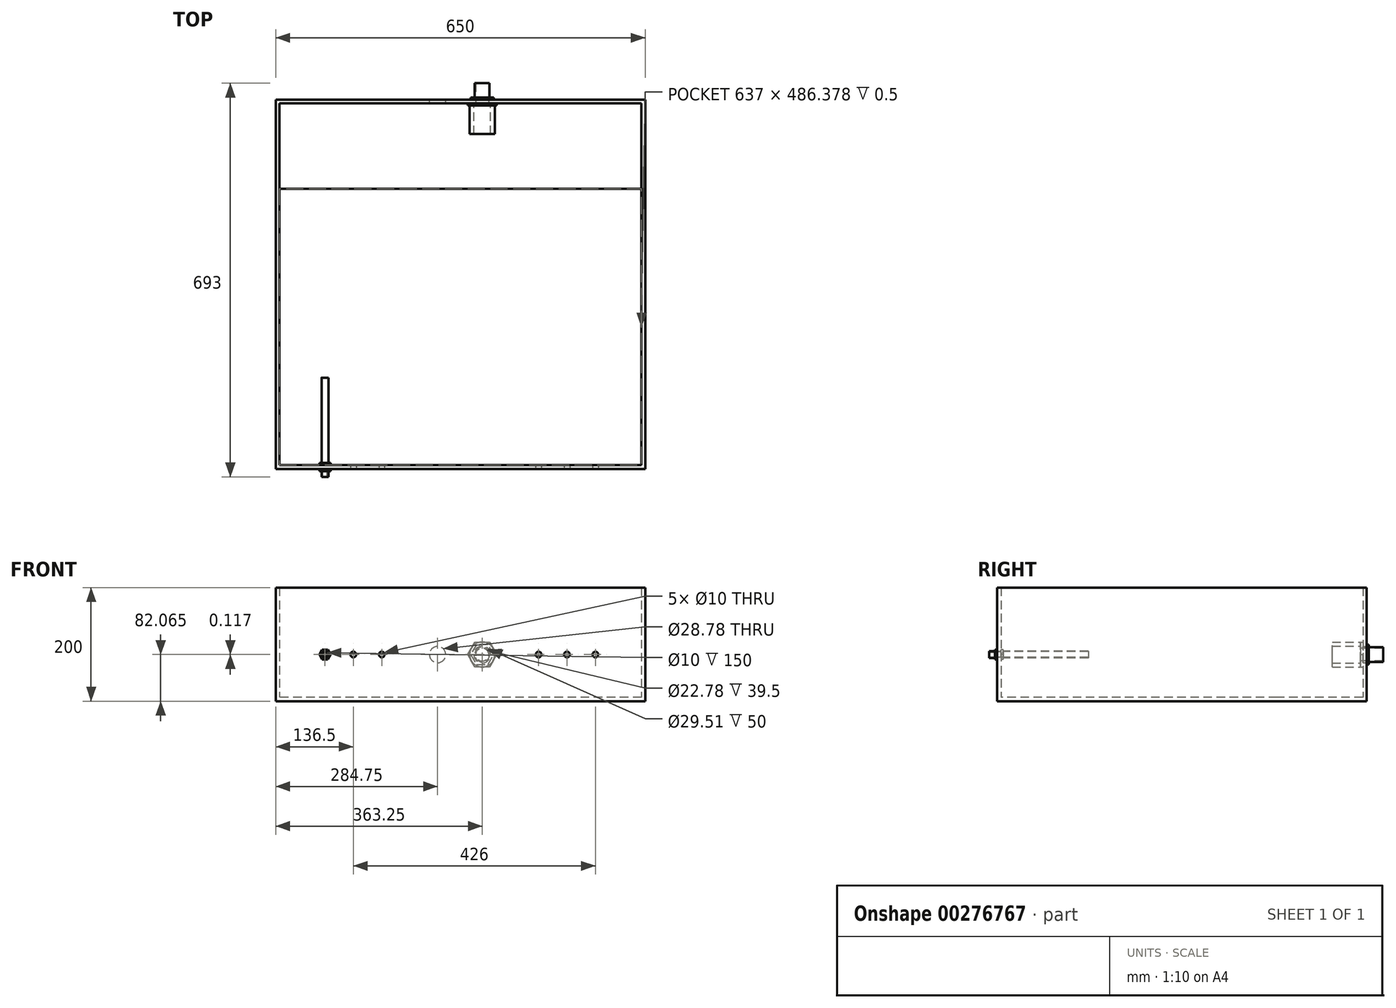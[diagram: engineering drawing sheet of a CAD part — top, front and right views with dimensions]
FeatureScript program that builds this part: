
annotation { "Feature Type Name" : "Feature", "Feature Type Description" : "" }
export const myFeature = defineFeature(function(context is Context, id is Id, definition is map)
    precondition{}
    {
        {
            var Q0;
            Q0=qCreatedBy(makeId("Top.planeOp"),FACE);
            var sketch = newSketch(context, id + "F0", { "sketchPlane" : qUnion([Q0])});
            skLineSegment(sketch, "E0.bottom", {"start": v(325, 325) * mm, "end": v(-325, 325) * mm});
            skLineSegment(sketch, "E0.top", {"start": v(325, -325) * mm, "end": v(-325, -325) * mm});
            skLineSegment(sketch, "E0.left", {"start": v(325, 325) * mm, "end": v(325, -325) * mm});
            skLineSegment(sketch, "E0.right", {"start": v(-325, 325) * mm, "end": v(-325, -325) * mm});
            skPoint(sketch, "E0.middle", {"position": v(0, 0) * mm});
            skSolve(sketch);
        }
        {
            var Q0;
            Q0=makeQuery(id+"F0.imprint","IMPRINT",FACE,{"disambiguationData":[TD([[makeQuery(id+"F0.imprint","IMPRINT",EDGE,{"derivedFrom":sQuery(id+"F0.wireOp",EDGE,"cca13281-c8a4-43dd-b4c7-58c42d9eb948.0")}),1.0]])]});
            var Q1;
            Q1=makeQuery(id+"F0.imprint","IMPRINT",FACE,{"disambiguationData":[TD([[makeQuery(id+"F0.imprint","IMPRINT",EDGE,{"derivedFrom":sQuery(id+"F0.wireOp",EDGE,"E0.bottom")}),1.0]])]});
            extrude(context, id + "F1", {"entities" : qUnion([Q0, Q1]), "depth" : 200 * mm});
        }
        {
            var Q0;
            Q0=makeQuery(id+"F1.opExtrude","CAP_FACE",FACE,{"disambiguationData":[OSD([sQuery(id+"F0.wireOp",EDGE,"E0.bottom"),sQuery(id+"F0.wireOp",EDGE,"E0.top"),sQuery(id+"F0.wireOp",EDGE,"E0.left"),sQuery(id+"F0.wireOp",EDGE,"E0.right")])],"isStart":false});
            shell(context, id + "F2", {"entities" : qUnion([Q0]), "thickness" : 2.5 * mm});
        }
        {
            var Q0;
            Q0=makeQuery(id+"F2.opShell","OFFSET_FACE",FACE,{"disambiguationData":[OSD([sQuery(id+"F0.wireOp",EDGE,"E0.bottom"),sQuery(id+"F0.wireOp",EDGE,"E0.top"),sQuery(id+"F0.wireOp",EDGE,"E0.left"),sQuery(id+"F0.wireOp",EDGE,"E0.right")])]});
            extrude(context, id + "F3", {"entities" : qUnion([Q0]), "depth" : 197.5 * mm});
        }
        {
            var Q0;
            Q0=makeQuery(id+"F3.opExtrude","CAP_FACE",FACE,{"disambiguationData":[OSD([sQuery(id+"F0.wireOp",EDGE,"E0.bottom"),sQuery(id+"F0.wireOp",EDGE,"E0.top"),sQuery(id+"F0.wireOp",EDGE,"E0.left"),sQuery(id+"F0.wireOp",EDGE,"E0.right")])],"isStart":false});
            shell(context, id + "F4", {"entities" : qUnion([Q0]), "thickness" : 4 * mm});
        }
        {
            var Q0;
            Q0=makeQuery(id+"F4.opShell","OFFSET_FACE",FACE,{"disambiguationData":[OSD([sQuery(id+"F0.wireOp",EDGE,"E0.bottom"),sQuery(id+"F0.wireOp",EDGE,"E0.top"),sQuery(id+"F0.wireOp",EDGE,"E0.left"),sQuery(id+"F0.wireOp",EDGE,"E0.right")])]});
            var sketch = newSketch(context, id + "F5", { "sketchPlane" : qUnion([Q0])});
            skLineSegment(sketch, "E1.bottom", {"start": v(450, 167.88) * mm, "end": v(-450, 167.88) * mm});
            skLineSegment(sketch, "E1.top", {"start": v(450, -167.88) * mm, "end": v(-450, -167.88) * mm});
            skLineSegment(sketch, "E1.left", {"start": v(450, 167.88) * mm, "end": v(450, -167.88) * mm});
            skLineSegment(sketch, "E1.right", {"start": v(-450, 167.88) * mm, "end": v(-450, -167.88) * mm});
            skPoint(sketch, "E1.middle", {"position": v(0, 0) * mm});
            skLineSegment(sketch, "E2.bottom", {"start": v(318.5, 318.5) * mm, "end": v(-318.5, 318.5) * mm});
            skLineSegment(sketch, "E2.top", {"start": v(318.5, -318.5) * mm, "end": v(-318.5, -318.5) * mm});
            skLineSegment(sketch, "E2.left", {"start": v(318.5, 318.5) * mm, "end": v(318.5, -318.5) * mm});
            skLineSegment(sketch, "E2.right", {"start": v(-318.5, 318.5) * mm, "end": v(-318.5, -318.5) * mm});
            skSolve(sketch);
        }
        {
            var Q0;
            Q0=makeQuery(id+"F5.imprint","IMPRINT",FACE,{"disambiguationData":[TD([[makeQuery(id+"F5.imprint","IMPRINT",EDGE,{"derivedFrom":sQuery(id+"F5.wireOp",EDGE,"E1.bottom")}),-1.0]])]});
            extrude(context, id + "F6", {"entities" : qUnion([Q0]), "operationType" : NewBodyOperationType.ADD, "depth" : 0.5 * mm});
        }
        {
            var Q0;
            Q0=makeQuery(id+"F1.opExtrude","SWEPT_FACE",FACE,{"disambiguationData":[OSD([sQuery(id+"F0.wireOp",EDGE,"E0.top")])]});
            var sketch = newSketch(context, id + "F7", { "sketchPlane" : qUnion([Q0])});
            skLineSegment(sketch, "E3.top", {"start": v(300, 6.5) * mm, "end": v(-300, 6.5) * mm, "construction": true});
            skPoint(sketch, "E3.middle", {"position": v(0, 100) * mm});
            skPoint(sketch, "E3.middle.positionSnap0", {"position": v(-325, 100) * mm});
            skPoint(sketch, "E3.centerSnap0", {"position": v(-325, 100) * mm});
            skLineSegment(sketch, "E4", {"start": v(-300, 6.5) * mm, "end": v(-300, 251.45) * mm, "construction": true});
            skLineSegment(sketch, "E5", {"start": v(-300, 251.45) * mm, "end": v(300, 251.45) * mm, "construction": true});
            skLineSegment(sketch, "E6", {"start": v(300, 251.45) * mm, "end": v(300, 6.5) * mm, "construction": true});
            skLineSegment(sketch, "E7", {"start": v(-300, 82.18) * mm, "end": v(-238.5, 82.18) * mm, "construction": true});
            skLineSegment(sketch, "E8", {"start": v(-238.5, 82.18) * mm, "end": v(-238.5, 6.5) * mm, "construction": true});
            skCircle(sketch, "E9", {"center": v(-238.5, 82.18) * mm, "radius": 5 * mm});
            skCircle(sketch, "E10.1.0.0", {"center": v(-188.5, 82.18) * mm, "radius": 5 * mm});
            skCircle(sketch, "E10.2.0.0", {"center": v(-138.5, 82.18) * mm, "radius": 5 * mm});
            skLineSegment(sketch, "E10.direction1", {"start": v(-238.5, 82.18) * mm, "end": v(-188.5, 82.18) * mm, "construction": true});
            skLineSegment(sketch, "E11", {"start": v(300, 82.07) * mm, "end": v(237.5, 82.07) * mm, "construction": true});
            skLineSegment(sketch, "E12", {"start": v(237.5, 82.07) * mm, "end": v(237.5, 6.5) * mm, "construction": true});
            skCircle(sketch, "E13", {"center": v(237.5, 82.07) * mm, "radius": 5 * mm});
            skCircle(sketch, "E14.1.0.0", {"center": v(187.5, 82.07) * mm, "radius": 5 * mm});
            skCircle(sketch, "E14.2.0.0", {"center": v(137.5, 82.07) * mm, "radius": 5 * mm});
            skLineSegment(sketch, "E14.direction1", {"start": v(237.5, 82.07) * mm, "end": v(187.5, 82.07) * mm, "construction": true});
            skSolve(sketch);
        }
        {
            var Q0;
            Q0=qSketchRegion(id+"F7",true);
            extrude(context, id + "F8", {"entities" : qUnion([Q0]), "operationType" : NewBodyOperationType.REMOVE, "oppositeDirection" : true, "depth" : 25 * mm});
        }
        {
            var Q0;
            Q0=makeQuery(id+"F1.opExtrude","SWEPT_FACE",FACE,{"disambiguationData":[OSD([sQuery(id+"F0.wireOp",EDGE,"E0.bottom")])]});
            var sketch = newSketch(context, id + "F9", { "sketchPlane" : qUnion([Q0])});
            skLineSegment(sketch, "E15", {"start": v(-300, 251.45) * mm, "end": v(-300, 6.5) * mm, "construction": true});
            skLineSegment(sketch, "E16", {"start": v(-300, 6.5) * mm, "end": v(300, 6.5) * mm, "construction": true});
            skLineSegment(sketch, "E17", {"start": v(300, 6.5) * mm, "end": v(300, 251.45) * mm, "construction": true});
            skLineSegment(sketch, "E18", {"start": v(300, 251.45) * mm, "end": v(-300, 251.45) * mm, "construction": true});
            skLineSegment(sketch, "E19", {"start": v(40.25, 6.5) * mm, "end": v(40.25, 82.07) * mm, "construction": true});
            skLineSegment(sketch, "E20", {"start": v(40.25, 82.06) * mm, "end": v(300, 82.07) * mm, "construction": true});
            skCircle(sketch, "E21", {"center": v(40.25, 82.07) * mm, "radius": 14.39 * mm});
            skCircle(sketch, "E22.1.0.0", {"center": v(-38.25, 82.07) * mm, "radius": 14.39 * mm});
            skLineSegment(sketch, "E22.direction1", {"start": v(40.25, 82.07) * mm, "end": v(-38.25, 82.07) * mm, "construction": true});
            skSolve(sketch);
        }
        {
            var Q0;
            Q0=qSketchRegion(id+"F9",true);
            extrude(context, id + "F10", {"entities" : qUnion([Q0]), "operationType" : NewBodyOperationType.REMOVE, "oppositeDirection" : true, "depth" : 15 * mm});
        }
        {
            var Q0;
            Q0=makeQuery(id+"F1.opExtrude","SWEPT_FACE",FACE,{"disambiguationData":[OSD([sQuery(id+"F0.wireOp",EDGE,"E0.top")])]});
            var sketch = newSketch(context, id + "F11", { "sketchPlane" : qUnion([Q0])});
            skCircle(sketch, "E23", {"center": v(-238.5, 82.18) * mm, "radius": 4 * mm});
            skCircle(sketch, "E24.cCircle", {"center": v(-238.5, 82.18) * mm, "radius": 8.5 * mm, "construction": true});
            skLineSegment(sketch, "E24.0", {"start": v(-243.4, 90.68) * mm, "end": v(-233.6, 90.68) * mm});
            skLineSegment(sketch, "E24.1", {"start": v(-233.6, 90.68) * mm, "end": v(-228.69, 82.18) * mm});
            skLineSegment(sketch, "E24.2", {"start": v(-228.69, 82.18) * mm, "end": v(-233.6, 73.68) * mm});
            skLineSegment(sketch, "E24.3", {"start": v(-233.6, 73.68) * mm, "end": v(-243.4, 73.68) * mm});
            skLineSegment(sketch, "E24.4", {"start": v(-243.4, 73.68) * mm, "end": v(-248.31, 82.18) * mm});
            skLineSegment(sketch, "E24.5", {"start": v(-248.31, 82.18) * mm, "end": v(-243.4, 90.68) * mm});
            skPoint(sketch, "E24.0.midPoint", {"position": v(-238.5, 90.68) * mm});
            skSolve(sketch);
        }
        {
            var Q0;
            Q0=qSketchRegion(id+"F11",true);
            extrude(context, id + "F12", {"entities" : qUnion([Q0]), "depth" : 4 * mm});
        }
        {
            var Q0;
            Q0=makeQuery(id+"F12.opExtrude","CAP_FACE",FACE,{"disambiguationData":[OSD([sQuery(id+"F11.wireOp",EDGE,"E23"),sQuery(id+"F11.wireOp",EDGE,"E24.0"),sQuery(id+"F11.wireOp",EDGE,"E24.1"),sQuery(id+"F11.wireOp",EDGE,"E24.2"),sQuery(id+"F11.wireOp",EDGE,"E24.3"),sQuery(id+"F11.wireOp",EDGE,"E24.4"),sQuery(id+"F11.wireOp",EDGE,"E24.5")])],"isStart":false});
            var sketch = newSketch(context, id + "F13", { "sketchPlane" : qUnion([Q0])});
            skCircle(sketch, "E25", {"center": v(-238.5, 82.18) * mm, "radius": 6 * mm});
            skCircle(sketch, "E26", {"center": v(-238.5, 82.18) * mm, "radius": 4 * mm});
            skSolve(sketch);
        }
        {
            var Q0;
            Q0=qSketchRegion(id+"F13",true);
            extrude(context, id + "F14", {"entities" : qUnion([Q0]), "operationType" : NewBodyOperationType.ADD, "depth" : 10 * mm});
        }
        {
            var Q0;
            Q0=makeQuery(id+"F12.opExtrude","CAP_FACE",FACE,{"disambiguationData":[OSD([sQuery(id+"F11.wireOp",EDGE,"E23"),sQuery(id+"F11.wireOp",EDGE,"E24.0"),sQuery(id+"F11.wireOp",EDGE,"E24.1"),sQuery(id+"F11.wireOp",EDGE,"E24.2"),sQuery(id+"F11.wireOp",EDGE,"E24.3"),sQuery(id+"F11.wireOp",EDGE,"E24.4"),sQuery(id+"F11.wireOp",EDGE,"E24.5")])],"isStart":true});
            var sketch = newSketch(context, id + "F15", { "sketchPlane" : qUnion([Q0])});
            skCircle(sketch, "E27", {"center": v(238.5, 82.18) * mm, "radius": 5 * mm});
            skCircle(sketch, "E28", {"center": v(238.5, 82.18) * mm, "radius": 4 * mm});
            skSolve(sketch);
        }
        {
            var Q0;
            Q0=qSketchRegion(id+"F15",true);
            extrude(context, id + "F16", {"entities" : qUnion([Q0]), "operationType" : NewBodyOperationType.ADD, "depth" : 6.5 * mm});
        }
        {
            var Q0;
            Q0=makeQuery(id+"F16.opExtrude","CAP_FACE",FACE,{"disambiguationData":[OSD([sQuery(id+"F15.wireOp",EDGE,"E27"),sQuery(id+"F15.wireOp",EDGE,"E28")])],"isStart":false});
            var sketch = newSketch(context, id + "F17", { "sketchPlane" : qUnion([Q0])});
            skCircle(sketch, "E29.cCircle", {"center": v(238.5, 82.18) * mm, "radius": 8.5 * mm, "construction": true});
            skLineSegment(sketch, "E29.0", {"start": v(233.6, 90.68) * mm, "end": v(243.4, 90.68) * mm});
            skLineSegment(sketch, "E29.1", {"start": v(243.4, 90.68) * mm, "end": v(248.31, 82.18) * mm});
            skLineSegment(sketch, "E29.2", {"start": v(248.31, 82.18) * mm, "end": v(243.4, 73.68) * mm});
            skLineSegment(sketch, "E29.3", {"start": v(243.4, 73.68) * mm, "end": v(233.6, 73.68) * mm});
            skLineSegment(sketch, "E29.4", {"start": v(233.6, 73.68) * mm, "end": v(228.69, 82.18) * mm});
            skLineSegment(sketch, "E29.5", {"start": v(228.69, 82.18) * mm, "end": v(233.6, 90.68) * mm});
            skPoint(sketch, "E29.0.midPoint", {"position": v(238.5, 90.68) * mm});
            skCircle(sketch, "E30", {"center": v(238.5, 82.18) * mm, "radius": 4 * mm});
            skSolve(sketch);
        }
        {
            var Q0;
            Q0=makeQuery(id+"F17.imprint","IMPRINT",FACE,{"disambiguationData":[TD([[makeQuery(id+"F17.imprint","IMPRINT",EDGE,{"derivedFrom":sQuery(id+"F17.wireOp",EDGE,"E30")}),1.0]])]});
            var Q1;
            Q1=makeQuery(id+"F17.imprint","IMPRINT",FACE,{"disambiguationData":[TD([[makeQuery(id+"F17.imprint","IMPRINT",EDGE,{"derivedFrom":sQuery(id+"F17.wireOp",EDGE,"E29.0")}),-1.0]])]});
            extrude(context, id + "F18", {"entities" : qUnion([Q0, Q1]), "operationType" : NewBodyOperationType.ADD, "depth" : 4 * mm});
        }
        {
            var Q0;
            Q0=makeQuery(id+"F18.opExtrude","CAP_FACE",FACE,{"disambiguationData":[OSD([sQuery(id+"F17.wireOp",EDGE,"E29.0"),sQuery(id+"F17.wireOp",EDGE,"E29.1"),sQuery(id+"F17.wireOp",EDGE,"E29.2"),sQuery(id+"F17.wireOp",EDGE,"E29.3"),sQuery(id+"F17.wireOp",EDGE,"E29.4"),sQuery(id+"F17.wireOp",EDGE,"E29.5"),sQuery(id+"F17.wireOp",EDGE,"E30")])],"isStart":false});
            var sketch = newSketch(context, id + "F19", { "sketchPlane" : qUnion([Q0])});
            skCircle(sketch, "E31", {"center": v(238.5, 82.18) * mm, "radius": 6 * mm});
            skCircle(sketch, "E32", {"center": v(238.5, 82.18) * mm, "radius": 5 * mm});
            skSolve(sketch);
        }
        {
            var Q0;
            Q0=qSketchRegion(id+"F19",true);
            extrude(context, id + "F20", {"entities" : qUnion([Q0]), "operationType" : NewBodyOperationType.ADD, "depth" : 150 * mm});
        }
        {
            var Q0;
            Q0=makeQuery(id+"F1.opExtrude","SWEPT_FACE",FACE,{"disambiguationData":[OSD([sQuery(id+"F0.wireOp",EDGE,"E0.bottom")])]});
            var sketch = newSketch(context, id + "F21", { "sketchPlane" : qUnion([Q0])});
            skCircle(sketch, "E33", {"center": v(-38.25, 82.07) * mm, "radius": 11.39 * mm});
            skCircle(sketch, "E34.cCircle", {"center": v(-38.25, 82.07) * mm, "radius": 17.48 * mm, "construction": true});
            skLineSegment(sketch, "E34.0", {"start": v(-48.34, 99.55) * mm, "end": v(-28.16, 99.55) * mm});
            skLineSegment(sketch, "E34.1", {"start": v(-28.16, 99.55) * mm, "end": v(-18.07, 82.07) * mm});
            skLineSegment(sketch, "E34.2", {"start": v(-18.07, 82.07) * mm, "end": v(-28.16, 64.58) * mm});
            skLineSegment(sketch, "E34.3", {"start": v(-28.16, 64.58) * mm, "end": v(-48.34, 64.58) * mm});
            skLineSegment(sketch, "E34.4", {"start": v(-48.34, 64.58) * mm, "end": v(-58.43, 82.06) * mm});
            skLineSegment(sketch, "E34.5", {"start": v(-58.43, 82.06) * mm, "end": v(-48.34, 99.55) * mm});
            skPoint(sketch, "E34.0.midPoint", {"position": v(-38.25, 99.55) * mm});
            skSolve(sketch);
        }
        {
            var Q0;
            Q0=qSketchRegion(id+"F21",true);
            extrude(context, id + "F22", {"entities" : qUnion([Q0]), "depth" : 4 * mm});
        }
        {
            var Q0;
            Q0=makeQuery(id+"F22.opExtrude","CAP_FACE",FACE,{"disambiguationData":[OSD([sQuery(id+"F21.wireOp",EDGE,"E33"),sQuery(id+"F21.wireOp",EDGE,"E34.0"),sQuery(id+"F21.wireOp",EDGE,"E34.1"),sQuery(id+"F21.wireOp",EDGE,"E34.2"),sQuery(id+"F21.wireOp",EDGE,"E34.3"),sQuery(id+"F21.wireOp",EDGE,"E34.4"),sQuery(id+"F21.wireOp",EDGE,"E34.5")])],"isStart":false});
            var sketch = newSketch(context, id + "F23", { "sketchPlane" : qUnion([Q0])});
            skCircle(sketch, "E35", {"center": v(-38.25, 82.07) * mm, "radius": 13.03 * mm});
            skCircle(sketch, "E36", {"center": v(-38.25, 82.07) * mm, "radius": 11.39 * mm});
            skSolve(sketch);
        }
        {
            var Q0;
            Q0=qSketchRegion(id+"F23",true);
            extrude(context, id + "F24", {"entities" : qUnion([Q0]), "operationType" : NewBodyOperationType.ADD, "depth" : 25 * mm});
        }
        {
            var Q0;
            Q0=makeQuery(id+"F22.opExtrude","CAP_FACE",FACE,{"disambiguationData":[OSD([sQuery(id+"F21.wireOp",EDGE,"E33"),sQuery(id+"F21.wireOp",EDGE,"E34.0"),sQuery(id+"F21.wireOp",EDGE,"E34.1"),sQuery(id+"F21.wireOp",EDGE,"E34.2"),sQuery(id+"F21.wireOp",EDGE,"E34.3"),sQuery(id+"F21.wireOp",EDGE,"E34.4"),sQuery(id+"F21.wireOp",EDGE,"E34.5")])],"isStart":true});
            var sketch = newSketch(context, id + "F25", { "sketchPlane" : qUnion([Q0])});
            skCircle(sketch, "E37", {"center": v(38.25, 82.07) * mm, "radius": 14.39 * mm});
            skCircle(sketch, "E38", {"center": v(38.25, 82.07) * mm, "radius": 11.39 * mm});
            skSolve(sketch);
        }
        {
            var Q0;
            Q0=qSketchRegion(id+"F25",true);
            extrude(context, id + "F26", {"entities" : qUnion([Q0]), "operationType" : NewBodyOperationType.ADD, "depth" : 6.5 * mm});
        }
        {
            var Q0;
            Q0=makeQuery(id+"F26.opExtrude","CAP_FACE",FACE,{"disambiguationData":[OSD([sQuery(id+"F25.wireOp",EDGE,"E37"),sQuery(id+"F25.wireOp",EDGE,"E38")])],"isStart":false});
            var sketch = newSketch(context, id + "F27", { "sketchPlane" : qUnion([Q0])});
            skCircle(sketch, "E39.cCircle", {"center": v(38.25, 82.07) * mm, "radius": 22 * mm, "construction": true});
            skLineSegment(sketch, "E39.0", {"start": v(25.55, 104.07) * mm, "end": v(50.95, 104.07) * mm});
            skLineSegment(sketch, "E39.1", {"start": v(50.95, 104.07) * mm, "end": v(63.66, 82.07) * mm});
            skLineSegment(sketch, "E39.2", {"start": v(63.66, 82.07) * mm, "end": v(50.95, 60.06) * mm});
            skLineSegment(sketch, "E39.3", {"start": v(50.95, 60.06) * mm, "end": v(25.55, 60.06) * mm});
            skLineSegment(sketch, "E39.4", {"start": v(25.55, 60.06) * mm, "end": v(12.84, 82.07) * mm});
            skLineSegment(sketch, "E39.5", {"start": v(12.84, 82.07) * mm, "end": v(25.55, 104.07) * mm});
            skPoint(sketch, "E39.0.midPoint", {"position": v(38.25, 104.07) * mm});
            skCircle(sketch, "E40", {"center": v(38.25, 82.07) * mm, "radius": 11.39 * mm});
            skSolve(sketch);
        }
        {
            var Q0;
            Q0=qSketchRegion(id+"F27",true);
            extrude(context, id + "F28", {"entities" : qUnion([Q0]), "operationType" : NewBodyOperationType.ADD, "depth" : 4 * mm});
        }
        {
            var Q0;
            Q0=makeQuery(id+"F28.opExtrude","CAP_FACE",FACE,{"disambiguationData":[OSD([sQuery(id+"F27.wireOp",EDGE,"E39.0"),sQuery(id+"F27.wireOp",EDGE,"E39.1"),sQuery(id+"F27.wireOp",EDGE,"E39.2"),sQuery(id+"F27.wireOp",EDGE,"E39.3"),sQuery(id+"F27.wireOp",EDGE,"E39.4"),sQuery(id+"F27.wireOp",EDGE,"E39.5"),sQuery(id+"F27.wireOp",EDGE,"E40")])],"isStart":false});
            var sketch = newSketch(context, id + "F29", { "sketchPlane" : qUnion([Q0])});
            skCircle(sketch, "E41", {"center": v(38.25, 82.07) * mm, "radius": 22 * mm});
            skCircle(sketch, "E42", {"center": v(38.25, 82.07) * mm, "radius": 14.76 * mm});
            skSolve(sketch);
        }
        {
            var Q0;
            Q0=qSketchRegion(id+"F29",true);
            extrude(context, id + "F30", {"entities" : qUnion([Q0]), "operationType" : NewBodyOperationType.ADD, "depth" : 50 * mm});
        }
    });
